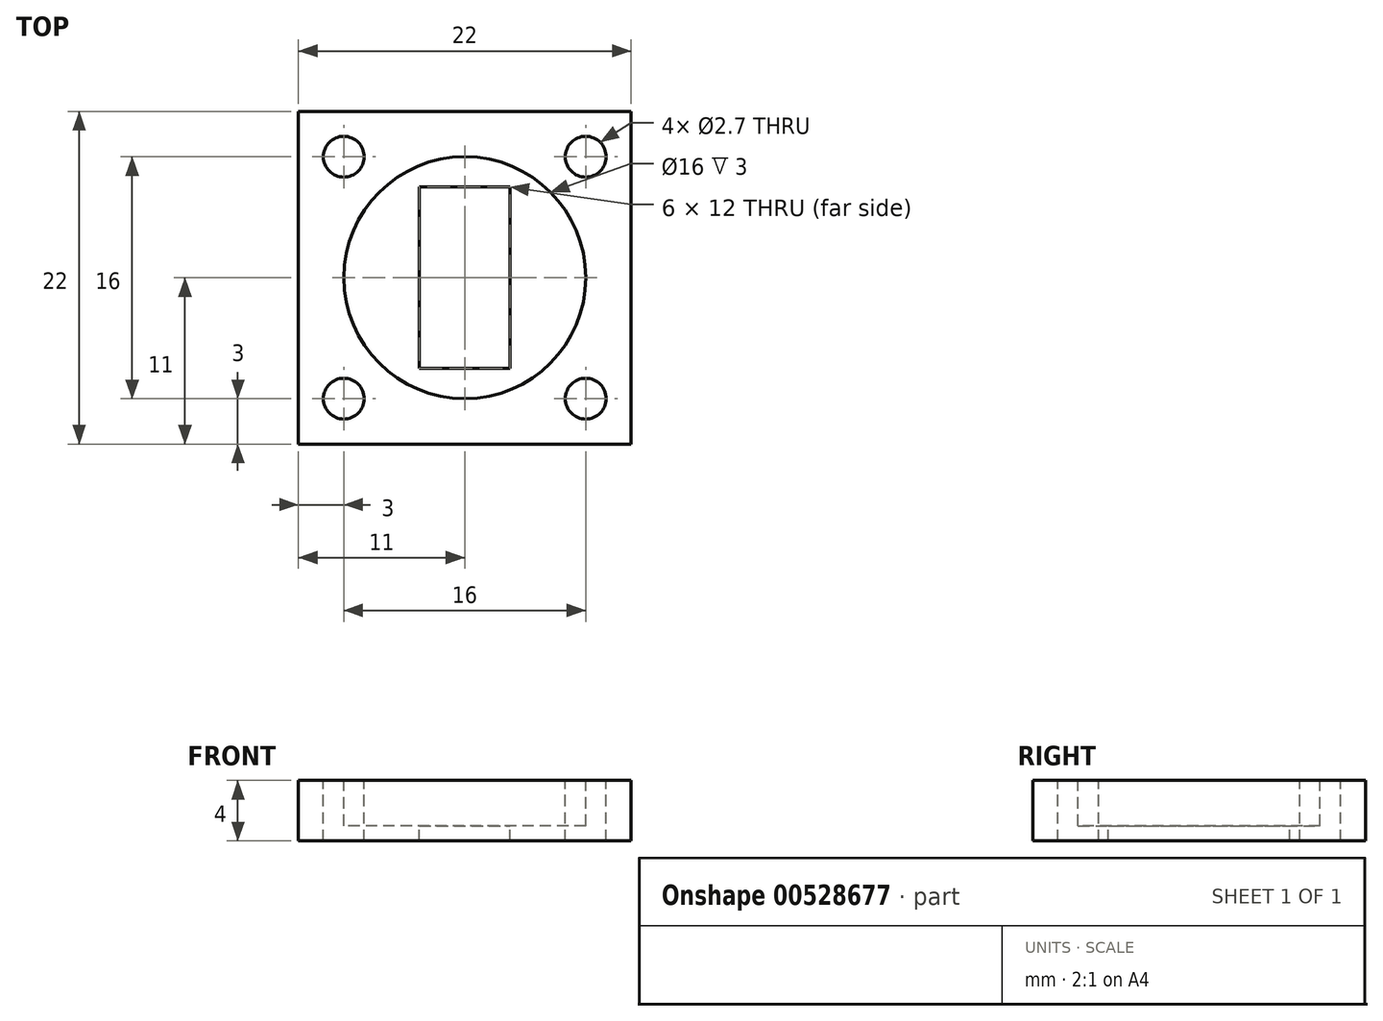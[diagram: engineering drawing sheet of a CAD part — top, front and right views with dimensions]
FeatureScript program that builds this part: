
annotation { "Feature Type Name" : "Feature", "Feature Type Description" : "" }
export const myFeature = defineFeature(function(context is Context, id is Id, definition is map)
    precondition{}
    {
        {
            var Q0;
            Q0=qCreatedBy(makeId("Top.planeOp"),FACE);
            var sketch = newSketch(context, id + "F0", { "sketchPlane" : qUnion([Q0])});
            skLineSegment(sketch, "E0.bottom", {"start": v(0, 0) * mm, "end": v(22, 0) * mm});
            skLineSegment(sketch, "E0.top", {"start": v(0, 22) * mm, "end": v(22, 22) * mm});
            skLineSegment(sketch, "E0.left", {"start": v(0, 0) * mm, "end": v(0, 22) * mm});
            skLineSegment(sketch, "E0.right", {"start": v(22, 0) * mm, "end": v(22, 22) * mm});
            skSolve(sketch);
        }
        {
            var Q0;
            Q0=makeQuery(id+"F0.imprint","IMPRINT",FACE,{"disambiguationData":[TD([[makeQuery(id+"F0.imprint","IMPRINT",EDGE,{"derivedFrom":sQuery(id+"F0.wireOp",EDGE,"E0.bottom")}),1.0]])]});
            extrude(context, id + "F1", {"entities" : qUnion([Q0]), "depth" : 4 * mm, "offsetDistance" : 25 * mm});
        }
        {
            var Q0;
            Q0=qCreatedBy(makeId("Top.planeOp"),FACE);
            cPlane(context, id + "F2", {"entities" : qUnion([Q0]), "cplaneType" : CPlaneType.OFFSET, "offset" : 1 * mm, "width" : 150 * mm, "height" : 150 * mm});
        }
        {
            var Q0;
            Q0=makeQuery(id+"F1.opExtrude","CAP_FACE",FACE,{"disambiguationData":[OSD([sQuery(id+"F0.wireOp",EDGE,"E0.bottom"),sQuery(id+"F0.wireOp",EDGE,"E0.top"),sQuery(id+"F0.wireOp",EDGE,"E0.left"),sQuery(id+"F0.wireOp",EDGE,"E0.right")])],"isStart":false});
            var sketch = newSketch(context, id + "F3", { "sketchPlane" : qUnion([Q0])});
            skCircle(sketch, "E1", {"center": v(3, 3) * mm, "radius": 1.35 * mm});
            skCircle(sketch, "E2.0.1.0", {"center": v(3, 19) * mm, "radius": 1.35 * mm});
            skCircle(sketch, "E2.1.0.0", {"center": v(19, 3) * mm, "radius": 1.35 * mm});
            skCircle(sketch, "E2.1.1.0", {"center": v(19, 19) * mm, "radius": 1.35 * mm});
            skLineSegment(sketch, "E2.direction1", {"start": v(3, 3) * mm, "end": v(19, 3) * mm, "construction": true});
            skLineSegment(sketch, "E2.direction2", {"start": v(3, 3) * mm, "end": v(3, 19) * mm, "construction": true});
            skSolve(sketch);
        }
        {
            var Q0;
            Q0=qSketchRegion(id+"F3",true);
            extrude(context, id + "F4", {"entities" : qUnion([Q0]), "operationType" : NewBodyOperationType.REMOVE, "endBound" : BoundingType.THROUGH_ALL, "oppositeDirection" : true, "depth" : 12 * mm, "offsetDistance" : 25 * mm});
        }
        {
            var Q0;
            Q0=makeQuery(id+"F3.imprint","IMPRINT",FACE,{"disambiguationData":[TD([[makeQuery(id+"F3.imprint","IMPRINT",EDGE,{"derivedFrom":sQuery(id+"F3.wireOp",EDGE,"E1")}),-1.0]])]});
            var sketch = newSketch(context, id + "F5", { "sketchPlane" : qUnion([Q0])});
            skLineSegment(sketch, "E3", {"start": v(0, 0) * mm, "end": v(11, 0) * mm, "construction": true});
            skLineSegment(sketch, "E4", {"start": v(11, 0) * mm, "end": v(11, 11) * mm, "construction": true});
            skCircle(sketch, "E5", {"center": v(11, 11) * mm, "radius": 8 * mm});
            skLineSegment(sketch, "E6.bottom", {"start": v(14, 17) * mm, "end": v(8, 17) * mm});
            skLineSegment(sketch, "E6.top", {"start": v(14, 5) * mm, "end": v(8, 5) * mm});
            skLineSegment(sketch, "E6.left", {"start": v(14, 17) * mm, "end": v(14, 5) * mm});
            skLineSegment(sketch, "E6.right", {"start": v(8, 17) * mm, "end": v(8, 5) * mm});
            skSolve(sketch);
        }
        {
            var Q0;
            Q0=makeQuery(id+"F5.imprint","IMPRINT",FACE,{"disambiguationData":[TD([[makeQuery(id+"F5.imprint","IMPRINT",EDGE,{"derivedFrom":sQuery(id+"F5.wireOp",EDGE,"E6.bottom")}),1.0]])]});
            extrude(context, id + "F6", {"entities" : qUnion([Q0]), "operationType" : NewBodyOperationType.REMOVE, "endBound" : BoundingType.THROUGH_ALL, "oppositeDirection" : true, "depth" : 25 * mm, "offsetDistance" : 25 * mm});
        }
        {
            var Q0;
            Q0=makeQuery(id+"F5.imprint","IMPRINT",FACE,{"disambiguationData":[TD([[makeQuery(id+"F5.imprint","IMPRINT",EDGE,{"derivedFrom":sQuery(id+"F5.wireOp",EDGE,"E5")}),1.0]])]});
            var Q1;
            Q1=qCreatedBy(id+"F2.planeOp",FACE);
            extrude(context, id + "F7", {"entities" : qUnion([Q0]), "operationType" : NewBodyOperationType.REMOVE, "endBound" : BoundingType.UP_TO_SURFACE, "oppositeDirection" : true, "depth" : 25 * mm, "endBoundEntityFace" : qUnion([Q1]), "offsetDistance" : 25 * mm});
        }
    });
